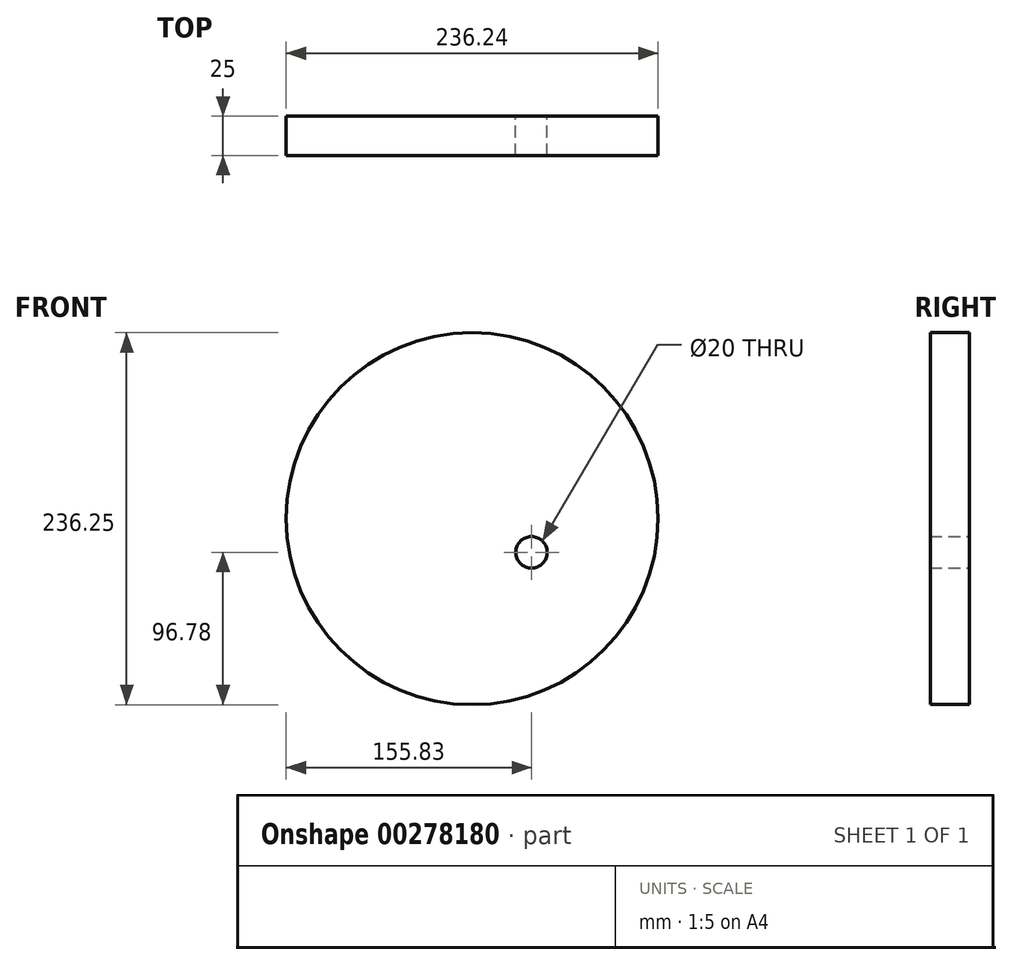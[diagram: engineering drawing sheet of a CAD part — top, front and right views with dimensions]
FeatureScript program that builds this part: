
annotation { "Feature Type Name" : "Feature", "Feature Type Description" : "" }
export const myFeature = defineFeature(function(context is Context, id is Id, definition is map)
    precondition{}
    {
        {
            var Q0;
            Q0=qCreatedBy(makeId("Front.planeOp"),FACE);
            var sketch = newSketch(context, id + "F0", { "sketchPlane" : qUnion([Q0])});
            skCircle(sketch, "E0", {"center": v(0, 0) * mm, "radius": 10 * mm});
            skCircle(sketch, "E1", {"center": v(-37.7, 21.34) * mm, "radius": 118.12 * mm});
            skSolve(sketch);
        }
        {
            var Q0;
            Q0 = qSketchRegion(id + "F0", true);
            extrude(context, id + "F1", {"entities" : qUnion([Q0]), "depth" : 25 * mm});
        }
    });
